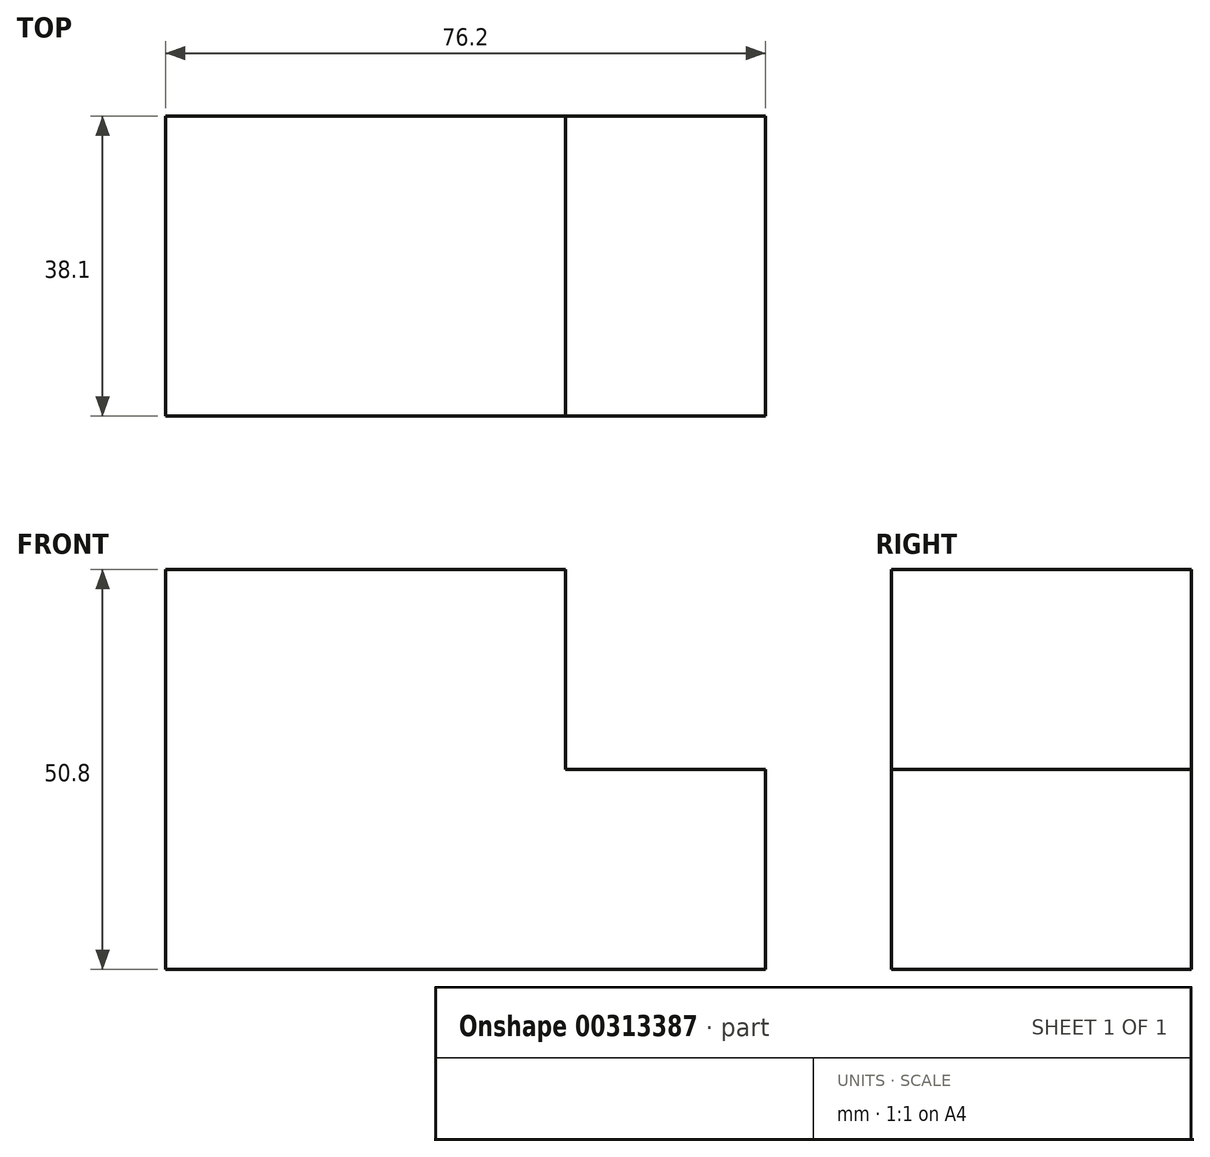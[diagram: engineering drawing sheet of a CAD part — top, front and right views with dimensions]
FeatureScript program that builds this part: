
annotation { "Feature Type Name" : "Feature", "Feature Type Description" : "" }
export const myFeature = defineFeature(function(context is Context, id is Id, definition is map)
    precondition{}
    {
        {
            var Q0;
            Q0=qCreatedBy(makeId("Front.planeOp"),FACE);
            var sketch = newSketch(context, id + "F0", { "sketchPlane" : qUnion([Q0])});
            skLineSegment(sketch, "E0", {"start": v(-36.86, -45.01) * mm, "end": v(39.34, -45.01) * mm});
            skLineSegment(sketch, "E1", {"start": v(39.34, -45.01) * mm, "end": v(39.34, -19.61) * mm});
            skLineSegment(sketch, "E2", {"start": v(39.34, -19.61) * mm, "end": v(13.94, -19.61) * mm});
            skLineSegment(sketch, "E3", {"start": v(13.94, -19.61) * mm, "end": v(13.94, 5.79) * mm});
            skLineSegment(sketch, "E4", {"start": v(13.94, 5.79) * mm, "end": v(-36.86, 5.79) * mm});
            skLineSegment(sketch, "E5", {"start": v(-36.86, 5.79) * mm, "end": v(-36.86, -45.01) * mm});
            skSolve(sketch);
        }
        {
            var Q0;
            Q0=makeQuery(id+"F0.imprint","IMPRINT",FACE,{"disambiguationData":[TD([[makeQuery(id+"F0.imprint","IMPRINT",EDGE,{"derivedFrom":sQuery(id+"F0.wireOp",EDGE,"E0")}),1.0]])]});
            extrude(context, id + "F1", {"entities" : qUnion([Q0]), "depth" : 38.1 * mm});
        }
    });
